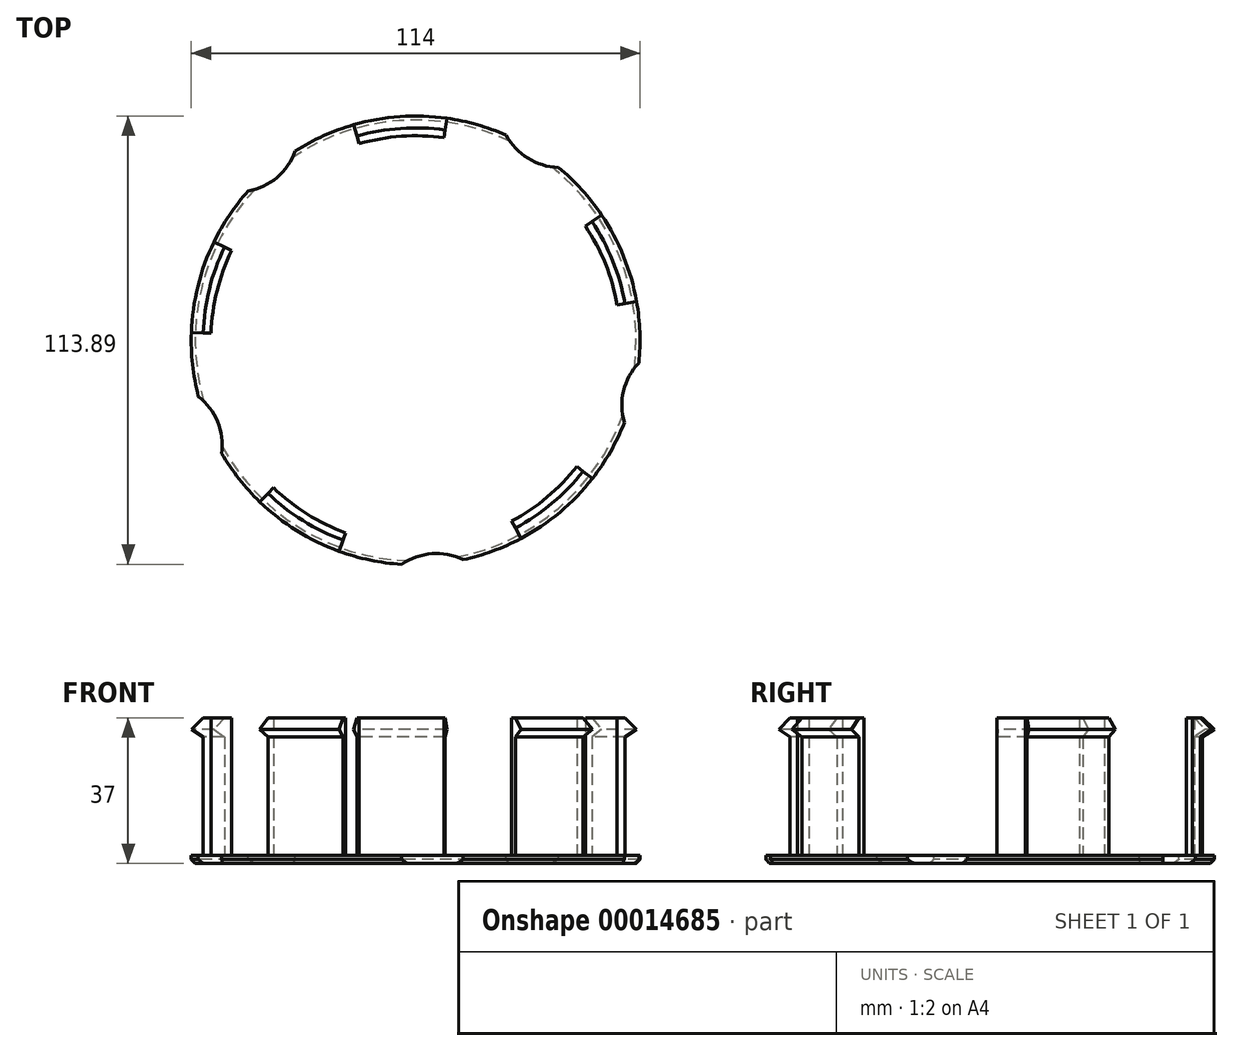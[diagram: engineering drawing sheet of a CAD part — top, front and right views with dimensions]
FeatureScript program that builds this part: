
annotation { "Feature Type Name" : "Feature", "Feature Type Description" : "" }
export const myFeature = defineFeature(function(context is Context, id is Id, definition is map)
    precondition{}
    {
        {
            var Q0;
            Q0=qCreatedBy(makeId("Top.planeOp"),FACE);
            var sketch = newSketch(context, id + "F0", { "sketchPlane" : qUnion([Q0])});
            skCircle(sketch, "E0", {"center": v(0, 0) * mm, "radius": 54 * mm});
            skCircle(sketch, "E1.0", {"center": v(0, 0) * mm, "radius": 52 * mm});
            skCircle(sketch, "E2.0", {"center": v(0, 0) * mm, "radius": 57 * mm});
            skLineSegment(sketch, "E3", {"start": v(0, 52) * mm, "end": v(0, 57) * mm});
            skLineSegment(sketch, "E4.1.0", {"start": v(-7.24, 51.5) * mm, "end": v(-7.93, 56.45) * mm});
            skLineSegment(sketch, "E4.2.0", {"start": v(-14.33, 49.99) * mm, "end": v(-15.71, 54.8) * mm});
            skLineSegment(sketch, "E4.3.0", {"start": v(-21.15, 47.5) * mm, "end": v(-23.18, 52.07) * mm});
            skLineSegment(sketch, "E4.4.0", {"start": v(-27.56, 44.1) * mm, "end": v(-30.2, 48.34) * mm});
            skLineSegment(sketch, "E4.5.0", {"start": v(-33.42, 39.83) * mm, "end": v(-36.64, 43.66) * mm});
            skLineSegment(sketch, "E4.6.0", {"start": v(-38.64, 34.8) * mm, "end": v(-42.36, 38.14) * mm});
            skLineSegment(sketch, "E4.7.0", {"start": v(-43.1, 29.08) * mm, "end": v(-47.26, 31.87) * mm});
            skLineSegment(sketch, "E4.8.0", {"start": v(-46.74, 22.8) * mm, "end": v(-51.23, 24.99) * mm});
            skLineSegment(sketch, "E4.9.0", {"start": v(-49.45, 16.07) * mm, "end": v(-54.21, 17.61) * mm});
            skLineSegment(sketch, "E5.1.10.0", {"start": v(-51.21, 9.03) * mm, "end": v(-56.13, 9.9) * mm});
            skLineSegment(sketch, "E5.1.11.0", {"start": v(-51.97, 1.81) * mm, "end": v(-56.97, 1.99) * mm});
            skLineSegment(sketch, "E5.1.12.0", {"start": v(-51.72, -5.44) * mm, "end": v(-56.69, -5.96) * mm});
            skLineSegment(sketch, "E5.1.13.0", {"start": v(-50.46, -12.58) * mm, "end": v(-55.3, -13.79) * mm});
            skLineSegment(sketch, "E5.1.14.0", {"start": v(-48.21, -19.48) * mm, "end": v(-52.85, -21.35) * mm});
            skLineSegment(sketch, "E5.1.15.0", {"start": v(-45.03, -26) * mm, "end": v(-49.36, -28.5) * mm});
            skLineSegment(sketch, "E5.1.16.0", {"start": v(-40.98, -32.01) * mm, "end": v(-44.92, -35.1) * mm});
            skLineSegment(sketch, "E5.1.17.0", {"start": v(-36.12, -37.4) * mm, "end": v(-39.6, -41) * mm});
            skLineSegment(sketch, "E5.1.18.0", {"start": v(-30.56, -42.07) * mm, "end": v(-33.5, -46.11) * mm});
            skLineSegment(sketch, "E5.1.19.0", {"start": v(-24.41, -45.91) * mm, "end": v(-26.76, -50.33) * mm});
            skLineSegment(sketch, "E6.1.20.0", {"start": v(-17.79, -48.86) * mm, "end": v(-19.5, -53.56) * mm});
            skLineSegment(sketch, "E6.1.21.0", {"start": v(-10.81, -50.86) * mm, "end": v(-11.85, -55.75) * mm});
            skLineSegment(sketch, "E6.1.22.0", {"start": v(-3.63, -51.87) * mm, "end": v(-3.98, -56.86) * mm});
            skLineSegment(sketch, "E6.1.23.0", {"start": v(3.63, -51.87) * mm, "end": v(3.98, -56.86) * mm});
            skLineSegment(sketch, "E6.1.24.0", {"start": v(10.81, -50.86) * mm, "end": v(11.85, -55.75) * mm});
            skLineSegment(sketch, "E7.1.25.0", {"start": v(17.79, -48.86) * mm, "end": v(19.5, -53.56) * mm});
            skLineSegment(sketch, "E8.1.26.0", {"start": v(24.41, -45.91) * mm, "end": v(26.76, -50.33) * mm});
            skLineSegment(sketch, "E8.1.27.0", {"start": v(30.56, -42.07) * mm, "end": v(33.5, -46.11) * mm});
            skLineSegment(sketch, "E8.1.28.0", {"start": v(36.12, -37.4) * mm, "end": v(39.6, -41) * mm});
            skLineSegment(sketch, "E8.1.29.0", {"start": v(40.98, -32.01) * mm, "end": v(44.92, -35.1) * mm});
            skLineSegment(sketch, "E9.1.30.0", {"start": v(45.03, -26) * mm, "end": v(49.36, -28.5) * mm});
            skLineSegment(sketch, "E9.1.31.0", {"start": v(48.21, -19.48) * mm, "end": v(52.85, -21.35) * mm});
            skLineSegment(sketch, "E9.1.32.0", {"start": v(50.46, -12.58) * mm, "end": v(55.3, -13.79) * mm});
            skLineSegment(sketch, "E9.1.33.0", {"start": v(51.72, -5.44) * mm, "end": v(56.69, -5.96) * mm});
            skLineSegment(sketch, "E9.1.34.0", {"start": v(51.97, 1.81) * mm, "end": v(56.97, 1.99) * mm});
            skLineSegment(sketch, "E10.1.35.0", {"start": v(51.21, 9.03) * mm, "end": v(56.13, 9.9) * mm});
            skLineSegment(sketch, "E10.1.36.0", {"start": v(49.45, 16.07) * mm, "end": v(54.21, 17.61) * mm});
            skLineSegment(sketch, "E10.1.37.0", {"start": v(46.74, 22.8) * mm, "end": v(51.23, 24.99) * mm});
            skLineSegment(sketch, "E10.1.38.0", {"start": v(43.1, 29.08) * mm, "end": v(47.26, 31.87) * mm});
            skLineSegment(sketch, "E10.1.39.0", {"start": v(38.64, 34.8) * mm, "end": v(42.36, 38.14) * mm});
            skCircle(sketch, "E11", {"center": v(36.65, 59.46) * mm, "radius": 15.5 * mm});
            skCircle(sketch, "E12.1.0", {"center": v(-45.23, 53.23) * mm, "radius": 15.5 * mm});
            skCircle(sketch, "E12.2.0", {"center": v(-64.6, -26.56) * mm, "radius": 15.5 * mm});
            skCircle(sketch, "E13.1.3.0", {"center": v(5.3, -69.65) * mm, "radius": 15.5 * mm});
            skCircle(sketch, "E13.1.4.0", {"center": v(67.88, -16.48) * mm, "radius": 15.5 * mm});
            skLineSegment(sketch, "E14.1.40.0", {"start": v(33.42, 39.83) * mm, "end": v(36.64, 43.66) * mm});
            skLineSegment(sketch, "E14.1.41.0", {"start": v(27.56, 44.1) * mm, "end": v(30.2, 48.34) * mm});
            skLineSegment(sketch, "E14.1.42.0", {"start": v(21.15, 47.5) * mm, "end": v(23.18, 52.07) * mm});
            skLineSegment(sketch, "E14.1.43.0", {"start": v(14.33, 49.99) * mm, "end": v(15.71, 54.8) * mm});
            skLineSegment(sketch, "E14.1.44.0", {"start": v(7.24, 51.5) * mm, "end": v(7.93, 56.45) * mm});
            skSolve(sketch);
        }
        {
            var Q0;
            {var subQ0=sQuery(id+"F0.wireOp",EDGE,"E3");var subQ1=sQuery(id+"F0.wireOp",EDGE,"E0");var subQ2=makeQuery(id+"F0.imprint","INTERSECT",VERTEX,{"derivedFrom":[subQ1,subQ0]});Q0=makeQuery(id+"F0.imprint","IMPRINT",FACE,{"disambiguationData":[TD([[makeQuery(id+"F0.imprint","IMPRINT",EDGE,{"disambiguationData":[TD([[subQ2,-1.0]])],"derivedFrom":subQ1}),1.0]])]});}
            var Q1;
            {var subQ1=sQuery(id+"F0.wireOp",EDGE,"E0");var subQ5=sQuery(id+"F0.wireOp",EDGE,"E4.1.0");var subQ6=makeQuery(id+"F0.imprint","INTERSECT",VERTEX,{"derivedFrom":[subQ1,subQ5]});Q1=makeQuery(id+"F0.imprint","IMPRINT",FACE,{"disambiguationData":[TD([[makeQuery(id+"F0.imprint","IMPRINT",EDGE,{"disambiguationData":[TD([[subQ6,-1.0]])],"derivedFrom":subQ1}),1.0]])]});}
            var Q2;
            {var subQ1=sQuery(id+"F0.wireOp",EDGE,"E0");var subQ5=sQuery(id+"F0.wireOp",EDGE,"E4.8.0");var subQ6=makeQuery(id+"F0.imprint","INTERSECT",VERTEX,{"derivedFrom":[subQ1,subQ5]});Q2=makeQuery(id+"F0.imprint","IMPRINT",FACE,{"disambiguationData":[TD([[makeQuery(id+"F0.imprint","IMPRINT",EDGE,{"disambiguationData":[TD([[subQ6,-1.0]])],"derivedFrom":subQ1}),1.0]])]});}
            var Q3;
            {var subQ1=sQuery(id+"F0.wireOp",EDGE,"E0");var subQ5=sQuery(id+"F0.wireOp",EDGE,"E3");var subQ6=makeQuery(id+"F0.imprint","INTERSECT",VERTEX,{"derivedFrom":[subQ1,subQ5]});Q3=makeQuery(id+"F0.imprint","IMPRINT",FACE,{"disambiguationData":[TD([[makeQuery(id+"F0.imprint","IMPRINT",EDGE,{"disambiguationData":[TD([[subQ6,-1.0]])],"derivedFrom":subQ1}),-1.0]])]});}
            var Q4;
            {var subQ1=sQuery(id+"F0.wireOp",EDGE,"E0");var subQ5=sQuery(id+"F0.wireOp",EDGE,"E4.1.0");var subQ6=makeQuery(id+"F0.imprint","INTERSECT",VERTEX,{"derivedFrom":[subQ1,subQ5]});Q4=makeQuery(id+"F0.imprint","IMPRINT",FACE,{"disambiguationData":[TD([[makeQuery(id+"F0.imprint","IMPRINT",EDGE,{"disambiguationData":[TD([[subQ6,-1.0]])],"derivedFrom":subQ1}),-1.0]])]});}
            var Q5;
            {var subQ0=sQuery(id+"F0.wireOp",EDGE,"E4.8.0");var subQ1=sQuery(id+"F0.wireOp",EDGE,"E0");var subQ2=makeQuery(id+"F0.imprint","INTERSECT",VERTEX,{"derivedFrom":[subQ1,subQ0]});Q5=makeQuery(id+"F0.imprint","IMPRINT",FACE,{"disambiguationData":[TD([[makeQuery(id+"F0.imprint","IMPRINT",EDGE,{"disambiguationData":[TD([[subQ2,-1.0]])],"derivedFrom":subQ1}),-1.0]])]});}
            var Q6;
            {var subQ1=sQuery(id+"F0.wireOp",EDGE,"E0");var subQ5=sQuery(id+"F0.wireOp",EDGE,"E4.9.0");var subQ6=makeQuery(id+"F0.imprint","INTERSECT",VERTEX,{"derivedFrom":[subQ1,subQ5]});Q6=makeQuery(id+"F0.imprint","IMPRINT",FACE,{"disambiguationData":[TD([[makeQuery(id+"F0.imprint","IMPRINT",EDGE,{"disambiguationData":[TD([[subQ6,-1.0]])],"derivedFrom":subQ1}),1.0]])]});}
            var Q7;
            {var subQ1=sQuery(id+"F0.wireOp",EDGE,"E0");var subQ5=sQuery(id+"F0.wireOp",EDGE,"E4.9.0");var subQ6=makeQuery(id+"F0.imprint","INTERSECT",VERTEX,{"derivedFrom":[subQ1,subQ5]});Q7=makeQuery(id+"F0.imprint","IMPRINT",FACE,{"disambiguationData":[TD([[makeQuery(id+"F0.imprint","IMPRINT",EDGE,{"disambiguationData":[TD([[subQ6,-1.0]])],"derivedFrom":subQ1}),-1.0]])]});}
            var Q8;
            {var subQ1=sQuery(id+"F0.wireOp",EDGE,"E0");var subQ5=sQuery(id+"F0.wireOp",EDGE,"E5.1.17.0");var subQ6=makeQuery(id+"F0.imprint","INTERSECT",VERTEX,{"derivedFrom":[subQ1,subQ5]});Q8=makeQuery(id+"F0.imprint","IMPRINT",FACE,{"disambiguationData":[TD([[makeQuery(id+"F0.imprint","IMPRINT",EDGE,{"disambiguationData":[TD([[subQ6,-1.0]])],"derivedFrom":subQ1}),-1.0]])]});}
            var Q9;
            {var subQ1=sQuery(id+"F0.wireOp",EDGE,"E0");var subQ5=sQuery(id+"F0.wireOp",EDGE,"E5.1.17.0");var subQ6=makeQuery(id+"F0.imprint","INTERSECT",VERTEX,{"derivedFrom":[subQ1,subQ5]});Q9=makeQuery(id+"F0.imprint","IMPRINT",FACE,{"disambiguationData":[TD([[makeQuery(id+"F0.imprint","IMPRINT",EDGE,{"disambiguationData":[TD([[subQ6,-1.0]])],"derivedFrom":subQ1}),1.0]])]});}
            var Q10;
            {var subQ1=sQuery(id+"F0.wireOp",EDGE,"E0");var subQ5=sQuery(id+"F0.wireOp",EDGE,"E5.1.10.0");var subQ6=makeQuery(id+"F0.imprint","INTERSECT",VERTEX,{"derivedFrom":[subQ1,subQ5]});Q10=makeQuery(id+"F0.imprint","IMPRINT",FACE,{"disambiguationData":[TD([[makeQuery(id+"F0.imprint","IMPRINT",EDGE,{"disambiguationData":[TD([[subQ6,-1.0]])],"derivedFrom":subQ1}),1.0]])]});}
            var Q11;
            {var subQ1=sQuery(id+"F0.wireOp",EDGE,"E0");var subQ5=sQuery(id+"F0.wireOp",EDGE,"E5.1.10.0");var subQ6=makeQuery(id+"F0.imprint","INTERSECT",VERTEX,{"derivedFrom":[subQ1,subQ5]});Q11=makeQuery(id+"F0.imprint","IMPRINT",FACE,{"disambiguationData":[TD([[makeQuery(id+"F0.imprint","IMPRINT",EDGE,{"disambiguationData":[TD([[subQ6,-1.0]])],"derivedFrom":subQ1}),-1.0]])]});}
            var Q12;
            {var subQ0=sQuery(id+"F0.wireOp",EDGE,"E14.1.44.0");var subQ1=sQuery(id+"F0.wireOp",EDGE,"E0");var subQ2=makeQuery(id+"F0.imprint","INTERSECT",VERTEX,{"derivedFrom":[subQ1,subQ0]});Q12=makeQuery(id+"F0.imprint","IMPRINT",FACE,{"disambiguationData":[TD([[makeQuery(id+"F0.imprint","IMPRINT",EDGE,{"disambiguationData":[TD([[subQ2,-1.0]])],"derivedFrom":subQ1}),1.0]])]});}
            var Q13;
            {var subQ0=sQuery(id+"F0.wireOp",EDGE,"E14.1.44.0");var subQ1=sQuery(id+"F0.wireOp",EDGE,"E0");var subQ2=makeQuery(id+"F0.imprint","INTERSECT",VERTEX,{"derivedFrom":[subQ1,subQ0]});Q13=makeQuery(id+"F0.imprint","IMPRINT",FACE,{"disambiguationData":[TD([[makeQuery(id+"F0.imprint","IMPRINT",EDGE,{"disambiguationData":[TD([[subQ2,-1.0]])],"derivedFrom":subQ1}),-1.0]])]});}
            var Q14;
            {var subQ1=sQuery(id+"F0.wireOp",EDGE,"E0");var subQ5=sQuery(id+"F0.wireOp",EDGE,"E10.1.37.0");var subQ6=makeQuery(id+"F0.imprint","INTERSECT",VERTEX,{"derivedFrom":[subQ1,subQ5]});Q14=makeQuery(id+"F0.imprint","IMPRINT",FACE,{"disambiguationData":[TD([[makeQuery(id+"F0.imprint","IMPRINT",EDGE,{"disambiguationData":[TD([[subQ6,-1.0]])],"derivedFrom":subQ1}),-1.0]])]});}
            var Q15;
            {var subQ1=sQuery(id+"F0.wireOp",EDGE,"E0");var subQ5=sQuery(id+"F0.wireOp",EDGE,"E10.1.37.0");var subQ6=makeQuery(id+"F0.imprint","INTERSECT",VERTEX,{"derivedFrom":[subQ1,subQ5]});Q15=makeQuery(id+"F0.imprint","IMPRINT",FACE,{"disambiguationData":[TD([[makeQuery(id+"F0.imprint","IMPRINT",EDGE,{"disambiguationData":[TD([[subQ6,-1.0]])],"derivedFrom":subQ1}),1.0]])]});}
            var Q16;
            {var subQ1=sQuery(id+"F0.wireOp",EDGE,"E0");var subQ5=sQuery(id+"F0.wireOp",EDGE,"E10.1.36.0");var subQ6=makeQuery(id+"F0.imprint","INTERSECT",VERTEX,{"derivedFrom":[subQ1,subQ5]});Q16=makeQuery(id+"F0.imprint","IMPRINT",FACE,{"disambiguationData":[TD([[makeQuery(id+"F0.imprint","IMPRINT",EDGE,{"disambiguationData":[TD([[subQ6,-1.0]])],"derivedFrom":subQ1}),-1.0]])]});}
            var Q17;
            {var subQ1=sQuery(id+"F0.wireOp",EDGE,"E0");var subQ5=sQuery(id+"F0.wireOp",EDGE,"E10.1.36.0");var subQ6=makeQuery(id+"F0.imprint","INTERSECT",VERTEX,{"derivedFrom":[subQ1,subQ5]});Q17=makeQuery(id+"F0.imprint","IMPRINT",FACE,{"disambiguationData":[TD([[makeQuery(id+"F0.imprint","IMPRINT",EDGE,{"disambiguationData":[TD([[subQ6,-1.0]])],"derivedFrom":subQ1}),1.0]])]});}
            var Q18;
            {var subQ1=sQuery(id+"F0.wireOp",EDGE,"E0");var subQ5=sQuery(id+"F0.wireOp",EDGE,"E10.1.35.0");var subQ6=makeQuery(id+"F0.imprint","INTERSECT",VERTEX,{"derivedFrom":[subQ1,subQ5]});Q18=makeQuery(id+"F0.imprint","IMPRINT",FACE,{"disambiguationData":[TD([[makeQuery(id+"F0.imprint","IMPRINT",EDGE,{"disambiguationData":[TD([[subQ6,-1.0]])],"derivedFrom":subQ1}),1.0]])]});}
            var Q19;
            {var subQ1=sQuery(id+"F0.wireOp",EDGE,"E0");var subQ5=sQuery(id+"F0.wireOp",EDGE,"E10.1.35.0");var subQ6=makeQuery(id+"F0.imprint","INTERSECT",VERTEX,{"derivedFrom":[subQ1,subQ5]});Q19=makeQuery(id+"F0.imprint","IMPRINT",FACE,{"disambiguationData":[TD([[makeQuery(id+"F0.imprint","IMPRINT",EDGE,{"disambiguationData":[TD([[subQ6,-1.0]])],"derivedFrom":subQ1}),-1.0]])]});}
            var Q20;
            {var subQ1=sQuery(id+"F0.wireOp",EDGE,"E0");var subQ5=sQuery(id+"F0.wireOp",EDGE,"E8.1.28.0");var subQ6=makeQuery(id+"F0.imprint","INTERSECT",VERTEX,{"derivedFrom":[subQ1,subQ5]});Q20=makeQuery(id+"F0.imprint","IMPRINT",FACE,{"disambiguationData":[TD([[makeQuery(id+"F0.imprint","IMPRINT",EDGE,{"disambiguationData":[TD([[subQ6,-1.0]])],"derivedFrom":subQ1}),-1.0]])]});}
            var Q21;
            {var subQ0=sQuery(id+"F0.wireOp",EDGE,"E8.1.28.0");var subQ1=sQuery(id+"F0.wireOp",EDGE,"E0");var subQ2=makeQuery(id+"F0.imprint","INTERSECT",VERTEX,{"derivedFrom":[subQ1,subQ0]});Q21=makeQuery(id+"F0.imprint","IMPRINT",FACE,{"disambiguationData":[TD([[makeQuery(id+"F0.imprint","IMPRINT",EDGE,{"disambiguationData":[TD([[subQ2,-1.0]])],"derivedFrom":subQ1}),1.0]])]});}
            var Q22;
            {var subQ1=sQuery(id+"F0.wireOp",EDGE,"E0");var subQ5=sQuery(id+"F0.wireOp",EDGE,"E8.1.27.0");var subQ6=makeQuery(id+"F0.imprint","INTERSECT",VERTEX,{"derivedFrom":[subQ1,subQ5]});Q22=makeQuery(id+"F0.imprint","IMPRINT",FACE,{"disambiguationData":[TD([[makeQuery(id+"F0.imprint","IMPRINT",EDGE,{"disambiguationData":[TD([[subQ6,-1.0]])],"derivedFrom":subQ1}),1.0]])]});}
            var Q23;
            {var subQ1=sQuery(id+"F0.wireOp",EDGE,"E0");var subQ5=sQuery(id+"F0.wireOp",EDGE,"E8.1.27.0");var subQ6=makeQuery(id+"F0.imprint","INTERSECT",VERTEX,{"derivedFrom":[subQ1,subQ5]});Q23=makeQuery(id+"F0.imprint","IMPRINT",FACE,{"disambiguationData":[TD([[makeQuery(id+"F0.imprint","IMPRINT",EDGE,{"disambiguationData":[TD([[subQ6,-1.0]])],"derivedFrom":subQ1}),-1.0]])]});}
            var Q24;
            {var subQ1=sQuery(id+"F0.wireOp",EDGE,"E0");var subQ5=sQuery(id+"F0.wireOp",EDGE,"E8.1.26.0");var subQ6=makeQuery(id+"F0.imprint","INTERSECT",VERTEX,{"derivedFrom":[subQ1,subQ5]});Q24=makeQuery(id+"F0.imprint","IMPRINT",FACE,{"disambiguationData":[TD([[makeQuery(id+"F0.imprint","IMPRINT",EDGE,{"disambiguationData":[TD([[subQ6,-1.0]])],"derivedFrom":subQ1}),-1.0]])]});}
            var Q25;
            {var subQ1=sQuery(id+"F0.wireOp",EDGE,"E0");var subQ5=sQuery(id+"F0.wireOp",EDGE,"E8.1.26.0");var subQ7=makeQuery(id+"F0.imprint","INTERSECT",VERTEX,{"derivedFrom":[subQ1,subQ5]});Q25=makeQuery(id+"F0.imprint","IMPRINT",FACE,{"disambiguationData":[TD([[makeQuery(id+"F0.imprint","IMPRINT",EDGE,{"disambiguationData":[TD([[subQ7,-1.0]])],"derivedFrom":subQ1}),1.0]])]});}
            var Q26;
            {var subQ1=sQuery(id+"F0.wireOp",EDGE,"E0");var subQ5=sQuery(id+"F0.wireOp",EDGE,"E5.1.19.0");var subQ6=makeQuery(id+"F0.imprint","INTERSECT",VERTEX,{"derivedFrom":[subQ1,subQ5]});Q26=makeQuery(id+"F0.imprint","IMPRINT",FACE,{"disambiguationData":[TD([[makeQuery(id+"F0.imprint","IMPRINT",EDGE,{"disambiguationData":[TD([[subQ6,-1.0]])],"derivedFrom":subQ1}),-1.0]])]});}
            var Q27;
            {var subQ1=sQuery(id+"F0.wireOp",EDGE,"E0");var subQ5=sQuery(id+"F0.wireOp",EDGE,"E5.1.19.0");var subQ6=makeQuery(id+"F0.imprint","INTERSECT",VERTEX,{"derivedFrom":[subQ1,subQ5]});Q27=makeQuery(id+"F0.imprint","IMPRINT",FACE,{"disambiguationData":[TD([[makeQuery(id+"F0.imprint","IMPRINT",EDGE,{"disambiguationData":[TD([[subQ6,-1.0]])],"derivedFrom":subQ1}),1.0]])]});}
            var Q28;
            {var subQ1=sQuery(id+"F0.wireOp",EDGE,"E0");var subQ5=sQuery(id+"F0.wireOp",EDGE,"E5.1.18.0");var subQ6=makeQuery(id+"F0.imprint","INTERSECT",VERTEX,{"derivedFrom":[subQ1,subQ5]});Q28=makeQuery(id+"F0.imprint","IMPRINT",FACE,{"disambiguationData":[TD([[makeQuery(id+"F0.imprint","IMPRINT",EDGE,{"disambiguationData":[TD([[subQ6,-1.0]])],"derivedFrom":subQ1}),1.0]])]});}
            var Q29;
            {var subQ1=sQuery(id+"F0.wireOp",EDGE,"E0");var subQ5=sQuery(id+"F0.wireOp",EDGE,"E5.1.18.0");var subQ6=makeQuery(id+"F0.imprint","INTERSECT",VERTEX,{"derivedFrom":[subQ1,subQ5]});Q29=makeQuery(id+"F0.imprint","IMPRINT",FACE,{"disambiguationData":[TD([[makeQuery(id+"F0.imprint","IMPRINT",EDGE,{"disambiguationData":[TD([[subQ6,-1.0]])],"derivedFrom":subQ1}),-1.0]])]});}
            extrude(context, id + "F1", {"entities" : qUnion([Q0, Q1, Q2, Q3, Q4, Q5, Q6, Q7, Q8, Q9, Q10, Q11, Q12, Q13, Q14, Q15, Q16, Q17, Q18, Q19, Q20, Q21, Q22, Q23, Q24, Q25, Q26, Q27, Q28, Q29]), "depth" : 35 * mm});
        }
        {
            var Q0;
            Q0=makeQuery(id+"F0.imprint","IMPRINT",FACE,{"disambiguationData":[TD([[makeQuery(id+"F0.imprint","IMPRINT",EDGE,{"derivedFrom":sQuery(id+"F0.wireOp",EDGE,"E0")}),-1.0]])]});
            var Q1;
            Q1=makeQuery(id+"F0.imprint","IMPRINT",FACE,{"disambiguationData":[TD([[makeQuery(id+"F0.imprint","IMPRINT",EDGE,{"derivedFrom":sQuery(id+"F0.wireOp",EDGE,"E0")}),1.0]])]});
            var Q2;
            Q2=makeQuery(id+"F0.imprint","IMPRINT",FACE,{"disambiguationData":[TD([[makeQuery(id+"F0.imprint","IMPRINT",EDGE,{"derivedFrom":sQuery(id+"F0.wireOp",EDGE,"6aa7c3f9-1c9a-4405-8abc-e9495ce803aa.0")}),1.0]])]});
            var Q3;
            {var subQ5=sQuery(id+"F0.wireOp",EDGE,"E0");var subQ7=sQuery(id+"F0.wireOp",EDGE,"E5.1.11.0");var subQ8=makeQuery(id+"F0.imprint","INTERSECT",VERTEX,{"derivedFrom":[subQ5,subQ7]});Q3=makeQuery(id+"F0.imprint","IMPRINT",FACE,{"disambiguationData":[TD([[makeQuery(id+"F0.imprint","IMPRINT",EDGE,{"disambiguationData":[TD([[subQ8,-1.0]])],"derivedFrom":subQ5}),-1.0]])]});}
            var Q4;
            {var subQ1=sQuery(id+"F0.wireOp",EDGE,"E5.1.13.0");var subQ6=sQuery(id+"F0.wireOp",EDGE,"E0");var subQ9=makeQuery(id+"F0.imprint","INTERSECT",VERTEX,{"derivedFrom":[subQ6,subQ1]});Q4=makeQuery(id+"F0.imprint","IMPRINT",FACE,{"disambiguationData":[TD([[makeQuery(id+"F0.imprint","IMPRINT",EDGE,{"disambiguationData":[TD([[subQ9,-1.0]])],"derivedFrom":subQ6}),-1.0]])]});}
            var Q5;
            {var subQ5=sQuery(id+"F0.wireOp",EDGE,"E0");var subQ7=sQuery(id+"F0.wireOp",EDGE,"E5.1.19.0");var subQ8=makeQuery(id+"F0.imprint","INTERSECT",VERTEX,{"derivedFrom":[subQ5,subQ7]});Q5=makeQuery(id+"F0.imprint","IMPRINT",FACE,{"disambiguationData":[TD([[makeQuery(id+"F0.imprint","IMPRINT",EDGE,{"disambiguationData":[TD([[subQ8,-1.0]])],"derivedFrom":subQ5}),-1.0]])]});}
            var Q6;
            {var subQ1=sQuery(id+"F0.wireOp",EDGE,"E6.1.21.0");var subQ6=sQuery(id+"F0.wireOp",EDGE,"E0");var subQ9=makeQuery(id+"F0.imprint","INTERSECT",VERTEX,{"derivedFrom":[subQ6,subQ1]});Q6=makeQuery(id+"F0.imprint","IMPRINT",FACE,{"disambiguationData":[TD([[makeQuery(id+"F0.imprint","IMPRINT",EDGE,{"disambiguationData":[TD([[subQ9,-1.0]])],"derivedFrom":subQ6}),-1.0]])]});}
            var Q7;
            {var subQ5=sQuery(id+"F0.wireOp",EDGE,"E0");var subQ7=sQuery(id+"F0.wireOp",EDGE,"E8.1.27.0");var subQ8=makeQuery(id+"F0.imprint","INTERSECT",VERTEX,{"derivedFrom":[subQ5,subQ7]});Q7=makeQuery(id+"F0.imprint","IMPRINT",FACE,{"disambiguationData":[TD([[makeQuery(id+"F0.imprint","IMPRINT",EDGE,{"disambiguationData":[TD([[subQ8,-1.0]])],"derivedFrom":subQ5}),-1.0]])]});}
            var Q8;
            {var subQ0=sQuery(id+"F0.wireOp",EDGE,"E9.1.30.0");var subQ1=sQuery(id+"F0.wireOp",EDGE,"E0");var subQ2=makeQuery(id+"F0.imprint","INTERSECT",VERTEX,{"derivedFrom":[subQ1,subQ0]});Q8=makeQuery(id+"F0.imprint","IMPRINT",FACE,{"disambiguationData":[TD([[makeQuery(id+"F0.imprint","IMPRINT",EDGE,{"disambiguationData":[TD([[subQ2,1.0]])],"derivedFrom":subQ1}),-1.0]])]});}
            var Q9;
            {var subQ5=sQuery(id+"F0.wireOp",EDGE,"E0");var subQ7=sQuery(id+"F0.wireOp",EDGE,"E10.1.35.0");var subQ8=makeQuery(id+"F0.imprint","INTERSECT",VERTEX,{"derivedFrom":[subQ5,subQ7]});Q9=makeQuery(id+"F0.imprint","IMPRINT",FACE,{"disambiguationData":[TD([[makeQuery(id+"F0.imprint","IMPRINT",EDGE,{"disambiguationData":[TD([[subQ8,-1.0]])],"derivedFrom":subQ5}),-1.0]])]});}
            var Q10;
            {var subQ1=sQuery(id+"F0.wireOp",EDGE,"E10.1.37.0");var subQ6=sQuery(id+"F0.wireOp",EDGE,"E0");var subQ9=makeQuery(id+"F0.imprint","INTERSECT",VERTEX,{"derivedFrom":[subQ6,subQ1]});Q10=makeQuery(id+"F0.imprint","IMPRINT",FACE,{"disambiguationData":[TD([[makeQuery(id+"F0.imprint","IMPRINT",EDGE,{"disambiguationData":[TD([[subQ9,-1.0]])],"derivedFrom":subQ6}),-1.0]])]});}
            var Q11;
            {var subQ5=sQuery(id+"F0.wireOp",EDGE,"E0");var subQ7=sQuery(id+"F0.wireOp",EDGE,"E4.3.0");var subQ8=makeQuery(id+"F0.imprint","INTERSECT",VERTEX,{"derivedFrom":[subQ5,subQ7]});Q11=makeQuery(id+"F0.imprint","IMPRINT",FACE,{"disambiguationData":[TD([[makeQuery(id+"F0.imprint","IMPRINT",EDGE,{"disambiguationData":[TD([[subQ8,-1.0]])],"derivedFrom":subQ5}),-1.0]])]});}
            var Q12;
            {var subQ1=sQuery(id+"F0.wireOp",EDGE,"E0");var subQ5=sQuery(id+"F0.wireOp",EDGE,"E4.5.0");var subQ8=makeQuery(id+"F0.imprint","INTERSECT",VERTEX,{"derivedFrom":[subQ1,subQ5]});Q12=makeQuery(id+"F0.imprint","IMPRINT",FACE,{"disambiguationData":[TD([[makeQuery(id+"F0.imprint","IMPRINT",EDGE,{"disambiguationData":[TD([[subQ8,-1.0]])],"derivedFrom":subQ1}),-1.0]])]});}
            var Q13;
            {var subQ1=sQuery(id+"F0.wireOp",EDGE,"E4.6.0");var subQ6=sQuery(id+"F0.wireOp",EDGE,"E0");var subQ9=makeQuery(id+"F0.imprint","INTERSECT",VERTEX,{"derivedFrom":[subQ6,subQ1]});Q13=makeQuery(id+"F0.imprint","IMPRINT",FACE,{"disambiguationData":[TD([[makeQuery(id+"F0.imprint","IMPRINT",EDGE,{"disambiguationData":[TD([[subQ9,-1.0]])],"derivedFrom":subQ6}),-1.0]])]});}
            var Q14;
            {var subQ5=sQuery(id+"F0.wireOp",EDGE,"E0");var subQ7=sQuery(id+"F0.wireOp",EDGE,"E4.4.0");var subQ8=makeQuery(id+"F0.imprint","INTERSECT",VERTEX,{"derivedFrom":[subQ5,subQ7]});Q14=makeQuery(id+"F0.imprint","IMPRINT",FACE,{"disambiguationData":[TD([[makeQuery(id+"F0.imprint","IMPRINT",EDGE,{"disambiguationData":[TD([[subQ8,-1.0]])],"derivedFrom":subQ5}),-1.0]])]});}
            var Q15;
            {var subQ1=sQuery(id+"F0.wireOp",EDGE,"E0");var subQ5=sQuery(id+"F0.wireOp",EDGE,"E14.1.42.0");var subQ8=makeQuery(id+"F0.imprint","INTERSECT",VERTEX,{"derivedFrom":[subQ1,subQ5]});Q15=makeQuery(id+"F0.imprint","IMPRINT",FACE,{"disambiguationData":[TD([[makeQuery(id+"F0.imprint","IMPRINT",EDGE,{"disambiguationData":[TD([[subQ8,-1.0]])],"derivedFrom":subQ1}),-1.0]])]});}
            var Q16;
            {var subQ3=sQuery(id+"F0.wireOp",EDGE,"E0");var subQ5=sQuery(id+"F0.wireOp",EDGE,"E14.1.40.0");var subQ6=makeQuery(id+"F0.imprint","INTERSECT",VERTEX,{"derivedFrom":[subQ3,subQ5]});Q16=makeQuery(id+"F0.imprint","IMPRINT",FACE,{"disambiguationData":[TD([[makeQuery(id+"F0.imprint","IMPRINT",EDGE,{"disambiguationData":[TD([[subQ6,-1.0]])],"derivedFrom":subQ3}),-1.0]])]});}
            var Q17;
            {var subQ1=sQuery(id+"F0.wireOp",EDGE,"E6.1.24.0");var subQ6=sQuery(id+"F0.wireOp",EDGE,"E0");var subQ9=makeQuery(id+"F0.imprint","INTERSECT",VERTEX,{"derivedFrom":[subQ6,subQ1]});Q17=makeQuery(id+"F0.imprint","IMPRINT",FACE,{"disambiguationData":[TD([[makeQuery(id+"F0.imprint","IMPRINT",EDGE,{"disambiguationData":[TD([[subQ9,-1.0]])],"derivedFrom":subQ6}),-1.0]])]});}
            var Q18;
            {var subQ5=sQuery(id+"F0.wireOp",EDGE,"E0");var subQ7=sQuery(id+"F0.wireOp",EDGE,"E6.1.22.0");var subQ8=makeQuery(id+"F0.imprint","INTERSECT",VERTEX,{"derivedFrom":[subQ5,subQ7]});Q18=makeQuery(id+"F0.imprint","IMPRINT",FACE,{"disambiguationData":[TD([[makeQuery(id+"F0.imprint","IMPRINT",EDGE,{"disambiguationData":[TD([[subQ8,-1.0]])],"derivedFrom":subQ5}),-1.0]])]});}
            var Q19;
            {var subQ1=sQuery(id+"F0.wireOp",EDGE,"E5.1.15.0");var subQ6=sQuery(id+"F0.wireOp",EDGE,"E0");var subQ9=makeQuery(id+"F0.imprint","INTERSECT",VERTEX,{"derivedFrom":[subQ6,subQ1]});Q19=makeQuery(id+"F0.imprint","IMPRINT",FACE,{"disambiguationData":[TD([[makeQuery(id+"F0.imprint","IMPRINT",EDGE,{"disambiguationData":[TD([[subQ9,-1.0]])],"derivedFrom":subQ6}),-1.0]])]});}
            var Q20;
            {var subQ5=sQuery(id+"F0.wireOp",EDGE,"E0");var subQ7=sQuery(id+"F0.wireOp",EDGE,"E9.1.31.0");var subQ8=makeQuery(id+"F0.imprint","INTERSECT",VERTEX,{"derivedFrom":[subQ5,subQ7]});Q20=makeQuery(id+"F0.imprint","IMPRINT",FACE,{"disambiguationData":[TD([[makeQuery(id+"F0.imprint","IMPRINT",EDGE,{"disambiguationData":[TD([[subQ8,-1.0]])],"derivedFrom":subQ5}),-1.0]])]});}
            var Q21;
            {var subQ5=sQuery(id+"F0.wireOp",EDGE,"E9.1.34.0");var subQ6=sQuery(id+"F0.wireOp",EDGE,"E0");var subQ7=makeQuery(id+"F0.imprint","INTERSECT",VERTEX,{"derivedFrom":[subQ6,subQ5]});Q21=makeQuery(id+"F0.imprint","IMPRINT",FACE,{"disambiguationData":[TD([[makeQuery(id+"F0.imprint","IMPRINT",EDGE,{"disambiguationData":[TD([[subQ7,1.0]])],"derivedFrom":subQ6}),-1.0]])]});}
            var Q22;
            {var subQ0=sQuery(id+"F0.wireOp",EDGE,"E1.0");var subQ1=makeQuery(id+"F0.imprint","INTERSECT",VERTEX,{"derivedFrom":[subQ0,sQuery(id+"F0.wireOp",EDGE,"E9.1.34.0")]});Q22=makeQuery(id+"F0.imprint","IMPRINT",FACE,{"disambiguationData":[TD([[makeQuery(id+"F0.imprint","IMPRINT",EDGE,{"disambiguationData":[TD([[subQ1,-1.0]])],"derivedFrom":subQ0}),1.0]])]});}
            var Q23;
            {var subQ1=sQuery(id+"F0.wireOp",EDGE,"E5.1.14.0");var subQ6=sQuery(id+"F0.wireOp",EDGE,"E0");var subQ9=makeQuery(id+"F0.imprint","INTERSECT",VERTEX,{"derivedFrom":[subQ6,subQ1]});Q23=makeQuery(id+"F0.imprint","IMPRINT",FACE,{"disambiguationData":[TD([[makeQuery(id+"F0.imprint","IMPRINT",EDGE,{"disambiguationData":[TD([[subQ9,-1.0]])],"derivedFrom":subQ6}),-1.0]])]});}
            var Q24;
            {var subQ1=sQuery(id+"F0.wireOp",EDGE,"E6.1.23.0");var subQ6=sQuery(id+"F0.wireOp",EDGE,"E0");var subQ9=makeQuery(id+"F0.imprint","INTERSECT",VERTEX,{"derivedFrom":[subQ6,subQ1]});Q24=makeQuery(id+"F0.imprint","IMPRINT",FACE,{"disambiguationData":[TD([[makeQuery(id+"F0.imprint","IMPRINT",EDGE,{"disambiguationData":[TD([[subQ9,-1.0]])],"derivedFrom":subQ6}),-1.0]])]});}
            var Q25;
            {var subQ1=sQuery(id+"F0.wireOp",EDGE,"E9.1.32.0");var subQ5=sQuery(id+"F0.wireOp",EDGE,"E0");var subQ6=makeQuery(id+"F0.imprint","INTERSECT",VERTEX,{"derivedFrom":[subQ5,subQ1]});Q25=makeQuery(id+"F0.imprint","IMPRINT",FACE,{"disambiguationData":[TD([[makeQuery(id+"F0.imprint","IMPRINT",EDGE,{"disambiguationData":[TD([[subQ6,-1.0]])],"derivedFrom":subQ5}),-1.0]])]});}
            var Q26;
            {var subQ1=sQuery(id+"F0.wireOp",EDGE,"E0");var subQ5=sQuery(id+"F0.wireOp",EDGE,"E14.1.41.0");var subQ8=makeQuery(id+"F0.imprint","INTERSECT",VERTEX,{"derivedFrom":[subQ1,subQ5]});Q26=makeQuery(id+"F0.imprint","IMPRINT",FACE,{"disambiguationData":[TD([[makeQuery(id+"F0.imprint","IMPRINT",EDGE,{"disambiguationData":[TD([[subQ8,-1.0]])],"derivedFrom":subQ1}),-1.0]])]});}
            extrude(context, id + "F2", {"entities" : qUnion([Q0, Q1, Q2, Q3, Q4, Q5, Q6, Q7, Q8, Q9, Q10, Q11, Q12, Q13, Q14, Q15, Q16, Q17, Q18, Q19, Q20, Q21, Q22, Q23, Q24, Q25, Q26]), "operationType" : NewBodyOperationType.ADD, "oppositeDirection" : true, "depth" : 2 * mm});
        }
        {
            var Q0;
            {var subQ1=sQuery(id+"F0.wireOp",EDGE,"E0");var subQ5=sQuery(id+"F0.wireOp",EDGE,"E10.1.35.0");var subQ6=makeQuery(id+"F0.imprint","INTERSECT",VERTEX,{"derivedFrom":[subQ1,subQ5]});Q0=makeQuery(id+"F0.imprint","IMPRINT",FACE,{"disambiguationData":[TD([[makeQuery(id+"F0.imprint","IMPRINT",EDGE,{"disambiguationData":[TD([[subQ6,-1.0]])],"derivedFrom":subQ1}),-1.0]])]});}
            var Q1;
            {var subQ1=sQuery(id+"F0.wireOp",EDGE,"E0");var subQ5=sQuery(id+"F0.wireOp",EDGE,"E10.1.36.0");var subQ6=makeQuery(id+"F0.imprint","INTERSECT",VERTEX,{"derivedFrom":[subQ1,subQ5]});Q1=makeQuery(id+"F0.imprint","IMPRINT",FACE,{"disambiguationData":[TD([[makeQuery(id+"F0.imprint","IMPRINT",EDGE,{"disambiguationData":[TD([[subQ6,-1.0]])],"derivedFrom":subQ1}),-1.0]])]});}
            var Q2;
            {var subQ1=sQuery(id+"F0.wireOp",EDGE,"E0");var subQ5=sQuery(id+"F0.wireOp",EDGE,"E10.1.37.0");var subQ6=makeQuery(id+"F0.imprint","INTERSECT",VERTEX,{"derivedFrom":[subQ1,subQ5]});Q2=makeQuery(id+"F0.imprint","IMPRINT",FACE,{"disambiguationData":[TD([[makeQuery(id+"F0.imprint","IMPRINT",EDGE,{"disambiguationData":[TD([[subQ6,-1.0]])],"derivedFrom":subQ1}),-1.0]])]});}
            var Q3;
            {var subQ0=sQuery(id+"F0.wireOp",EDGE,"E14.1.44.0");var subQ1=sQuery(id+"F0.wireOp",EDGE,"E0");var subQ2=makeQuery(id+"F0.imprint","INTERSECT",VERTEX,{"derivedFrom":[subQ1,subQ0]});Q3=makeQuery(id+"F0.imprint","IMPRINT",FACE,{"disambiguationData":[TD([[makeQuery(id+"F0.imprint","IMPRINT",EDGE,{"disambiguationData":[TD([[subQ2,-1.0]])],"derivedFrom":subQ1}),-1.0]])]});}
            var Q4;
            {var subQ1=sQuery(id+"F0.wireOp",EDGE,"E0");var subQ5=sQuery(id+"F0.wireOp",EDGE,"E3");var subQ6=makeQuery(id+"F0.imprint","INTERSECT",VERTEX,{"derivedFrom":[subQ1,subQ5]});Q4=makeQuery(id+"F0.imprint","IMPRINT",FACE,{"disambiguationData":[TD([[makeQuery(id+"F0.imprint","IMPRINT",EDGE,{"disambiguationData":[TD([[subQ6,-1.0]])],"derivedFrom":subQ1}),-1.0]])]});}
            var Q5;
            {var subQ1=sQuery(id+"F0.wireOp",EDGE,"E0");var subQ5=sQuery(id+"F0.wireOp",EDGE,"E4.1.0");var subQ6=makeQuery(id+"F0.imprint","INTERSECT",VERTEX,{"derivedFrom":[subQ1,subQ5]});Q5=makeQuery(id+"F0.imprint","IMPRINT",FACE,{"disambiguationData":[TD([[makeQuery(id+"F0.imprint","IMPRINT",EDGE,{"disambiguationData":[TD([[subQ6,-1.0]])],"derivedFrom":subQ1}),-1.0]])]});}
            var Q6;
            {var subQ1=sQuery(id+"F0.wireOp",EDGE,"E0");var subQ5=sQuery(id+"F0.wireOp",EDGE,"E4.8.0");var subQ6=makeQuery(id+"F0.imprint","INTERSECT",VERTEX,{"derivedFrom":[subQ1,subQ5]});Q6=makeQuery(id+"F0.imprint","IMPRINT",FACE,{"disambiguationData":[TD([[makeQuery(id+"F0.imprint","IMPRINT",EDGE,{"disambiguationData":[TD([[subQ6,-1.0]])],"derivedFrom":subQ1}),-1.0]])]});}
            var Q7;
            {var subQ1=sQuery(id+"F0.wireOp",EDGE,"E0");var subQ5=sQuery(id+"F0.wireOp",EDGE,"E4.9.0");var subQ6=makeQuery(id+"F0.imprint","INTERSECT",VERTEX,{"derivedFrom":[subQ1,subQ5]});Q7=makeQuery(id+"F0.imprint","IMPRINT",FACE,{"disambiguationData":[TD([[makeQuery(id+"F0.imprint","IMPRINT",EDGE,{"disambiguationData":[TD([[subQ6,-1.0]])],"derivedFrom":subQ1}),-1.0]])]});}
            var Q8;
            {var subQ1=sQuery(id+"F0.wireOp",EDGE,"E0");var subQ5=sQuery(id+"F0.wireOp",EDGE,"E5.1.10.0");var subQ6=makeQuery(id+"F0.imprint","INTERSECT",VERTEX,{"derivedFrom":[subQ1,subQ5]});Q8=makeQuery(id+"F0.imprint","IMPRINT",FACE,{"disambiguationData":[TD([[makeQuery(id+"F0.imprint","IMPRINT",EDGE,{"disambiguationData":[TD([[subQ6,-1.0]])],"derivedFrom":subQ1}),-1.0]])]});}
            var Q9;
            {var subQ1=sQuery(id+"F0.wireOp",EDGE,"E0");var subQ5=sQuery(id+"F0.wireOp",EDGE,"E5.1.17.0");var subQ6=makeQuery(id+"F0.imprint","INTERSECT",VERTEX,{"derivedFrom":[subQ1,subQ5]});Q9=makeQuery(id+"F0.imprint","IMPRINT",FACE,{"disambiguationData":[TD([[makeQuery(id+"F0.imprint","IMPRINT",EDGE,{"disambiguationData":[TD([[subQ6,-1.0]])],"derivedFrom":subQ1}),-1.0]])]});}
            var Q10;
            {var subQ1=sQuery(id+"F0.wireOp",EDGE,"E0");var subQ5=sQuery(id+"F0.wireOp",EDGE,"E5.1.18.0");var subQ6=makeQuery(id+"F0.imprint","INTERSECT",VERTEX,{"derivedFrom":[subQ1,subQ5]});Q10=makeQuery(id+"F0.imprint","IMPRINT",FACE,{"disambiguationData":[TD([[makeQuery(id+"F0.imprint","IMPRINT",EDGE,{"disambiguationData":[TD([[subQ6,-1.0]])],"derivedFrom":subQ1}),-1.0]])]});}
            var Q11;
            {var subQ1=sQuery(id+"F0.wireOp",EDGE,"E0");var subQ5=sQuery(id+"F0.wireOp",EDGE,"E5.1.19.0");var subQ6=makeQuery(id+"F0.imprint","INTERSECT",VERTEX,{"derivedFrom":[subQ1,subQ5]});Q11=makeQuery(id+"F0.imprint","IMPRINT",FACE,{"disambiguationData":[TD([[makeQuery(id+"F0.imprint","IMPRINT",EDGE,{"disambiguationData":[TD([[subQ6,-1.0]])],"derivedFrom":subQ1}),-1.0]])]});}
            var Q12;
            {var subQ1=sQuery(id+"F0.wireOp",EDGE,"E0");var subQ5=sQuery(id+"F0.wireOp",EDGE,"E8.1.26.0");var subQ6=makeQuery(id+"F0.imprint","INTERSECT",VERTEX,{"derivedFrom":[subQ1,subQ5]});Q12=makeQuery(id+"F0.imprint","IMPRINT",FACE,{"disambiguationData":[TD([[makeQuery(id+"F0.imprint","IMPRINT",EDGE,{"disambiguationData":[TD([[subQ6,-1.0]])],"derivedFrom":subQ1}),-1.0]])]});}
            var Q13;
            {var subQ1=sQuery(id+"F0.wireOp",EDGE,"E0");var subQ5=sQuery(id+"F0.wireOp",EDGE,"E8.1.27.0");var subQ6=makeQuery(id+"F0.imprint","INTERSECT",VERTEX,{"derivedFrom":[subQ1,subQ5]});Q13=makeQuery(id+"F0.imprint","IMPRINT",FACE,{"disambiguationData":[TD([[makeQuery(id+"F0.imprint","IMPRINT",EDGE,{"disambiguationData":[TD([[subQ6,-1.0]])],"derivedFrom":subQ1}),-1.0]])]});}
            var Q14;
            {var subQ1=sQuery(id+"F0.wireOp",EDGE,"E0");var subQ5=sQuery(id+"F0.wireOp",EDGE,"E8.1.28.0");var subQ6=makeQuery(id+"F0.imprint","INTERSECT",VERTEX,{"derivedFrom":[subQ1,subQ5]});Q14=makeQuery(id+"F0.imprint","IMPRINT",FACE,{"disambiguationData":[TD([[makeQuery(id+"F0.imprint","IMPRINT",EDGE,{"disambiguationData":[TD([[subQ6,-1.0]])],"derivedFrom":subQ1}),-1.0]])]});}
            var Q15;
            Q15=sQuery(id+"F0.wireOp",EDGE,"E2.0");
            extrude(context, id + "F3", {"entities" : qUnion([Q0, Q1, Q2, Q3, Q4, Q5, Q6, Q7, Q8, Q9, Q10, Q11, Q12, Q13, Q14]), "operationType" : NewBodyOperationType.REMOVE, "surfaceEntities" : qUnion([Q15]), "depth" : 32 * mm});
        }
        {
            var Q0;
            Q0=makeQuery(id+"F1.opExtrude","CAP_EDGE",EDGE,{"disambiguationData":[OSD([sQuery(id+"F0.wireOp",EDGE,"E2.0")])],"isStart":false});
            chamfer(context, id + "F4", {"entities" : qUnion([Q0]), "width" : 3 * mm, "tangentPropagation" : true});
        }
        {
            var Q0;
            {var subQ0=sQuery(id+"F0.wireOp",EDGE,"E2.0");var subQ1=makeQuery(id+"F0.imprint","INTERSECT",VERTEX,{"derivedFrom":[subQ0,sQuery(id+"F0.wireOp",EDGE,"E5.1.16.0")]});var subQ2=makeQuery(id+"F0.imprint","INTERSECT",VERTEX,{"derivedFrom":[subQ0,sQuery(id+"F0.wireOp",EDGE,"E5.1.17.0")]});var subQ3=makeQuery(id+"F0.imprint","INTERSECT",VERTEX,{"derivedFrom":[subQ0,sQuery(id+"F0.wireOp",EDGE,"E5.1.18.0")]});var subQ4=makeQuery(id+"F0.imprint","INTERSECT",VERTEX,{"derivedFrom":[subQ0,sQuery(id+"F0.wireOp",EDGE,"E5.1.19.0")]});var subQ5=makeQuery(id+"F0.imprint","INTERSECT",VERTEX,{"derivedFrom":[subQ0,sQuery(id+"F0.wireOp",EDGE,"E6.1.20.0")]});var subQ6=makeQuery(id+"F0.imprint","INTERSECT",VERTEX,{"derivedFrom":[subQ0,sQuery(id+"F0.wireOp",EDGE,"E6.1.21.0")]});var subQ7=makeQuery(id+"F0.imprint","INTERSECT",VERTEX,{"derivedFrom":[subQ0,sQuery(id+"F0.wireOp",EDGE,"E6.1.22.0")]});Q0=makeQuery(id+"F2.opExtrude","CAP_EDGE",EDGE,{"disambiguationData":[OSD([subQ0]),TDD([makeQuery(id+"F0.imprint","IMPRINT",EDGE,{"disambiguationData":[TD([[subQ1,1.0]])],"derivedFrom":subQ0}),makeQuery(id+"F0.imprint","IMPRINT",EDGE,{"disambiguationData":[TD([[subQ1,-1.0]])],"derivedFrom":subQ0}),makeQuery(id+"F0.imprint","IMPRINT",EDGE,{"disambiguationData":[TD([[subQ2,-1.0]])],"derivedFrom":subQ0}),makeQuery(id+"F0.imprint","IMPRINT",EDGE,{"disambiguationData":[TD([[subQ3,-1.0]])],"derivedFrom":subQ0}),makeQuery(id+"F0.imprint","IMPRINT",EDGE,{"disambiguationData":[TD([[subQ4,-1.0]])],"derivedFrom":subQ0}),makeQuery(id+"F0.imprint","IMPRINT",EDGE,{"disambiguationData":[TD([[subQ5,-1.0]])],"derivedFrom":subQ0}),makeQuery(id+"F0.imprint","IMPRINT",EDGE,{"disambiguationData":[TD([[subQ6,-1.0]])],"derivedFrom":subQ0}),makeQuery(id+"F0.imprint","IMPRINT",EDGE,{"disambiguationData":[TD([[subQ7,-1.0]])],"derivedFrom":subQ0})])],"isStart":false});}
            var Q1;
            {var subQ0=sQuery(id+"F0.wireOp",EDGE,"E2.0");var subQ1=makeQuery(id+"F0.imprint","INTERSECT",VERTEX,{"derivedFrom":[subQ0,sQuery(id+"F0.wireOp",EDGE,"E7.1.25.0")]});var subQ2=makeQuery(id+"F0.imprint","INTERSECT",VERTEX,{"derivedFrom":[subQ0,sQuery(id+"F0.wireOp",EDGE,"E8.1.26.0")]});var subQ3=makeQuery(id+"F0.imprint","INTERSECT",VERTEX,{"derivedFrom":[subQ0,sQuery(id+"F0.wireOp",EDGE,"E8.1.27.0")]});var subQ4=makeQuery(id+"F0.imprint","INTERSECT",VERTEX,{"derivedFrom":[subQ0,sQuery(id+"F0.wireOp",EDGE,"E8.1.28.0")]});var subQ5=makeQuery(id+"F0.imprint","INTERSECT",VERTEX,{"derivedFrom":[subQ0,sQuery(id+"F0.wireOp",EDGE,"E8.1.29.0")]});var subQ6=makeQuery(id+"F0.imprint","INTERSECT",VERTEX,{"derivedFrom":[subQ0,sQuery(id+"F0.wireOp",EDGE,"E9.1.30.0")]});var subQ7=makeQuery(id+"F0.imprint","INTERSECT",VERTEX,{"derivedFrom":[subQ0,sQuery(id+"F0.wireOp",EDGE,"E9.1.31.0")]});Q1=makeQuery(id+"F2.opExtrude","CAP_EDGE",EDGE,{"disambiguationData":[OSD([subQ0]),TDD([makeQuery(id+"F0.imprint","IMPRINT",EDGE,{"disambiguationData":[TD([[subQ1,1.0]])],"derivedFrom":subQ0}),makeQuery(id+"F0.imprint","IMPRINT",EDGE,{"disambiguationData":[TD([[subQ1,-1.0]])],"derivedFrom":subQ0}),makeQuery(id+"F0.imprint","IMPRINT",EDGE,{"disambiguationData":[TD([[subQ2,-1.0]])],"derivedFrom":subQ0}),makeQuery(id+"F0.imprint","IMPRINT",EDGE,{"disambiguationData":[TD([[subQ3,-1.0]])],"derivedFrom":subQ0}),makeQuery(id+"F0.imprint","IMPRINT",EDGE,{"disambiguationData":[TD([[subQ4,-1.0]])],"derivedFrom":subQ0}),makeQuery(id+"F0.imprint","IMPRINT",EDGE,{"disambiguationData":[TD([[subQ5,-1.0]])],"derivedFrom":subQ0}),makeQuery(id+"F0.imprint","IMPRINT",EDGE,{"disambiguationData":[TD([[subQ6,-1.0]])],"derivedFrom":subQ0}),makeQuery(id+"F0.imprint","IMPRINT",EDGE,{"disambiguationData":[TD([[subQ7,-1.0]])],"derivedFrom":subQ0})])],"isStart":false});}
            var Q2;
            {var subQ0=sQuery(id+"F0.wireOp",EDGE,"E2.0");var subQ1=makeQuery(id+"F0.imprint","INTERSECT",VERTEX,{"derivedFrom":[subQ0,sQuery(id+"F0.wireOp",EDGE,"E10.1.35.0")]});var subQ2=makeQuery(id+"F0.imprint","INTERSECT",VERTEX,{"derivedFrom":[subQ0,sQuery(id+"F0.wireOp",EDGE,"E9.1.34.0")]});var subQ3=makeQuery(id+"F0.imprint","INTERSECT",VERTEX,{"derivedFrom":[subQ0,sQuery(id+"F0.wireOp",EDGE,"E10.1.36.0")]});var subQ4=makeQuery(id+"F0.imprint","INTERSECT",VERTEX,{"derivedFrom":[subQ0,sQuery(id+"F0.wireOp",EDGE,"E10.1.37.0")]});var subQ5=makeQuery(id+"F0.imprint","INTERSECT",VERTEX,{"derivedFrom":[subQ0,sQuery(id+"F0.wireOp",EDGE,"E10.1.38.0")]});var subQ6=makeQuery(id+"F0.imprint","INTERSECT",VERTEX,{"derivedFrom":[subQ0,sQuery(id+"F0.wireOp",EDGE,"E10.1.39.0")]});var subQ7=makeQuery(id+"F0.imprint","INTERSECT",VERTEX,{"derivedFrom":[subQ0,sQuery(id+"F0.wireOp",EDGE,"E14.1.40.0")]});Q2=makeQuery(id+"F2.opExtrude","CAP_EDGE",EDGE,{"disambiguationData":[OSD([subQ0]),TDD([makeQuery(id+"F0.imprint","IMPRINT",EDGE,{"disambiguationData":[TD([[subQ2,-1.0]])],"derivedFrom":subQ0}),makeQuery(id+"F0.imprint","IMPRINT",EDGE,{"disambiguationData":[TD([[subQ1,-1.0]])],"derivedFrom":subQ0}),makeQuery(id+"F0.imprint","IMPRINT",EDGE,{"disambiguationData":[TD([[subQ3,-1.0]])],"derivedFrom":subQ0}),makeQuery(id+"F0.imprint","IMPRINT",EDGE,{"disambiguationData":[TD([[subQ4,-1.0]])],"derivedFrom":subQ0}),makeQuery(id+"F0.imprint","IMPRINT",EDGE,{"disambiguationData":[TD([[subQ5,-1.0]])],"derivedFrom":subQ0}),makeQuery(id+"F0.imprint","IMPRINT",EDGE,{"disambiguationData":[TD([[subQ6,-1.0]])],"derivedFrom":subQ0}),makeQuery(id+"F0.imprint","IMPRINT",EDGE,{"disambiguationData":[TD([[subQ7,-1.0]])],"derivedFrom":subQ0}),makeQuery(id+"F0.imprint","IMPRINT",EDGE,{"disambiguationData":[TD([[subQ2,1.0]])],"derivedFrom":subQ0})])],"isStart":false});}
            var Q3;
            {var subQ0=sQuery(id+"F0.wireOp",EDGE,"E2.0");var subQ1=makeQuery(id+"F0.imprint","INTERSECT",VERTEX,{"derivedFrom":[subQ0,sQuery(id+"F0.wireOp",EDGE,"E14.1.43.0")]});var subQ3=makeQuery(id+"F0.imprint","INTERSECT",VERTEX,{"derivedFrom":[subQ0,sQuery(id+"F0.wireOp",EDGE,"E3")]});var subQ4=makeQuery(id+"F0.imprint","INTERSECT",VERTEX,{"derivedFrom":[subQ0,sQuery(id+"F0.wireOp",EDGE,"E4.1.0")]});var subQ5=makeQuery(id+"F0.imprint","INTERSECT",VERTEX,{"derivedFrom":[subQ0,sQuery(id+"F0.wireOp",EDGE,"E4.2.0")]});var subQ6=makeQuery(id+"F0.imprint","INTERSECT",VERTEX,{"derivedFrom":[subQ0,sQuery(id+"F0.wireOp",EDGE,"E4.3.0")]});var subQ7=makeQuery(id+"F0.imprint","INTERSECT",VERTEX,{"derivedFrom":[subQ0,sQuery(id+"F0.wireOp",EDGE,"E4.4.0")]});Q3=makeQuery(id+"F2.opExtrude","CAP_EDGE",EDGE,{"disambiguationData":[OSD([subQ0]),TDD([makeQuery(id+"F0.imprint","IMPRINT",EDGE,{"disambiguationData":[TD([[subQ1,1.0]])],"derivedFrom":subQ0}),makeQuery(id+"F0.imprint","IMPRINT",EDGE,{"disambiguationData":[TD([[subQ1,-1.0]])],"derivedFrom":subQ0}),makeQuery(id+"F0.imprint","IMPRINT",EDGE,{"disambiguationData":[TD([[subQ3,1.0]])],"derivedFrom":subQ0}),makeQuery(id+"F0.imprint","IMPRINT",EDGE,{"disambiguationData":[TD([[subQ3,-1.0]])],"derivedFrom":subQ0}),makeQuery(id+"F0.imprint","IMPRINT",EDGE,{"disambiguationData":[TD([[subQ4,-1.0]])],"derivedFrom":subQ0}),makeQuery(id+"F0.imprint","IMPRINT",EDGE,{"disambiguationData":[TD([[subQ5,-1.0]])],"derivedFrom":subQ0}),makeQuery(id+"F0.imprint","IMPRINT",EDGE,{"disambiguationData":[TD([[subQ6,-1.0]])],"derivedFrom":subQ0}),makeQuery(id+"F0.imprint","IMPRINT",EDGE,{"disambiguationData":[TD([[subQ7,-1.0]])],"derivedFrom":subQ0})])],"isStart":false});}
            var Q4;
            {var subQ0=sQuery(id+"F0.wireOp",EDGE,"E2.0");var subQ1=makeQuery(id+"F0.imprint","INTERSECT",VERTEX,{"derivedFrom":[subQ0,sQuery(id+"F0.wireOp",EDGE,"E4.7.0")]});var subQ2=makeQuery(id+"F0.imprint","INTERSECT",VERTEX,{"derivedFrom":[subQ0,sQuery(id+"F0.wireOp",EDGE,"E4.8.0")]});var subQ3=makeQuery(id+"F0.imprint","INTERSECT",VERTEX,{"derivedFrom":[subQ0,sQuery(id+"F0.wireOp",EDGE,"E4.9.0")]});var subQ4=makeQuery(id+"F0.imprint","INTERSECT",VERTEX,{"derivedFrom":[subQ0,sQuery(id+"F0.wireOp",EDGE,"E5.1.10.0")]});var subQ5=makeQuery(id+"F0.imprint","INTERSECT",VERTEX,{"derivedFrom":[subQ0,sQuery(id+"F0.wireOp",EDGE,"E5.1.11.0")]});var subQ6=makeQuery(id+"F0.imprint","INTERSECT",VERTEX,{"derivedFrom":[subQ0,sQuery(id+"F0.wireOp",EDGE,"E5.1.12.0")]});var subQ7=makeQuery(id+"F0.imprint","INTERSECT",VERTEX,{"derivedFrom":[subQ0,sQuery(id+"F0.wireOp",EDGE,"E5.1.13.0")]});Q4=makeQuery(id+"F2.opExtrude","CAP_EDGE",EDGE,{"disambiguationData":[OSD([subQ0]),TDD([makeQuery(id+"F0.imprint","IMPRINT",EDGE,{"disambiguationData":[TD([[subQ1,1.0]])],"derivedFrom":subQ0}),makeQuery(id+"F0.imprint","IMPRINT",EDGE,{"disambiguationData":[TD([[subQ1,-1.0]])],"derivedFrom":subQ0}),makeQuery(id+"F0.imprint","IMPRINT",EDGE,{"disambiguationData":[TD([[subQ2,-1.0]])],"derivedFrom":subQ0}),makeQuery(id+"F0.imprint","IMPRINT",EDGE,{"disambiguationData":[TD([[subQ3,-1.0]])],"derivedFrom":subQ0}),makeQuery(id+"F0.imprint","IMPRINT",EDGE,{"disambiguationData":[TD([[subQ4,-1.0]])],"derivedFrom":subQ0}),makeQuery(id+"F0.imprint","IMPRINT",EDGE,{"disambiguationData":[TD([[subQ5,-1.0]])],"derivedFrom":subQ0}),makeQuery(id+"F0.imprint","IMPRINT",EDGE,{"disambiguationData":[TD([[subQ6,-1.0]])],"derivedFrom":subQ0}),makeQuery(id+"F0.imprint","IMPRINT",EDGE,{"disambiguationData":[TD([[subQ7,-1.0]])],"derivedFrom":subQ0})])],"isStart":false});}
            chamfer(context, id + "F5", {"entities" : qUnion([Q0, Q1, Q2, Q3, Q4]), "width" : 1 * mm});
        }
        {
            var Q0;
            {var subQ0=sQuery(id+"F0.wireOp",EDGE,"E0");var subQ1=makeQuery(id+"F0.imprint","INTERSECT",VERTEX,{"derivedFrom":[subQ0,sQuery(id+"F0.wireOp",EDGE,"E3")]});var subQ2=makeQuery(id+"F0.imprint","INTERSECT",VERTEX,{"derivedFrom":[subQ0,sQuery(id+"F0.wireOp",EDGE,"E4.1.0")]});Q0=makeQuery(id+"F3.boolean.opBoolean","COPY",EDGE,{"derivedFrom":makeQuery(id+"F3.opExtrude","CAP_EDGE",EDGE,{"disambiguationData":[OSD([subQ0]),TDD([makeQuery(id+"F0.imprint","IMPRINT",EDGE,{"disambiguationData":[TD([[makeQuery(id+"F0.imprint","INTERSECT",VERTEX,{"derivedFrom":[subQ0,sQuery(id+"F0.wireOp",EDGE,"E14.1.44.0")]}),-1.0]])],"derivedFrom":subQ0}),makeQuery(id+"F0.imprint","IMPRINT",EDGE,{"disambiguationData":[TD([[subQ1,-1.0]])],"derivedFrom":subQ0}),makeQuery(id+"F0.imprint","IMPRINT",EDGE,{"disambiguationData":[TD([[subQ2,-1.0]])],"derivedFrom":subQ0})])],"isStart":false})});}
            var Q1;
            {var subQ0=sQuery(id+"F0.wireOp",EDGE,"E0");var subQ1=makeQuery(id+"F0.imprint","INTERSECT",VERTEX,{"derivedFrom":[subQ0,sQuery(id+"F0.wireOp",EDGE,"E10.1.36.0")]});var subQ2=makeQuery(id+"F0.imprint","INTERSECT",VERTEX,{"derivedFrom":[subQ0,sQuery(id+"F0.wireOp",EDGE,"E10.1.37.0")]});Q1=makeQuery(id+"F3.boolean.opBoolean","COPY",EDGE,{"derivedFrom":makeQuery(id+"F3.opExtrude","CAP_EDGE",EDGE,{"disambiguationData":[OSD([subQ0]),TDD([makeQuery(id+"F0.imprint","IMPRINT",EDGE,{"disambiguationData":[TD([[makeQuery(id+"F0.imprint","INTERSECT",VERTEX,{"derivedFrom":[subQ0,sQuery(id+"F0.wireOp",EDGE,"E10.1.35.0")]}),-1.0]])],"derivedFrom":subQ0}),makeQuery(id+"F0.imprint","IMPRINT",EDGE,{"disambiguationData":[TD([[subQ1,-1.0]])],"derivedFrom":subQ0}),makeQuery(id+"F0.imprint","IMPRINT",EDGE,{"disambiguationData":[TD([[subQ2,-1.0]])],"derivedFrom":subQ0})])],"isStart":false})});}
            var Q2;
            {var subQ0=sQuery(id+"F0.wireOp",EDGE,"E0");var subQ1=makeQuery(id+"F0.imprint","INTERSECT",VERTEX,{"derivedFrom":[subQ0,sQuery(id+"F0.wireOp",EDGE,"E8.1.27.0")]});var subQ2=makeQuery(id+"F0.imprint","INTERSECT",VERTEX,{"derivedFrom":[subQ0,sQuery(id+"F0.wireOp",EDGE,"E8.1.28.0")]});Q2=makeQuery(id+"F3.boolean.opBoolean","COPY",EDGE,{"derivedFrom":makeQuery(id+"F3.opExtrude","CAP_EDGE",EDGE,{"disambiguationData":[OSD([subQ0]),TDD([makeQuery(id+"F0.imprint","IMPRINT",EDGE,{"disambiguationData":[TD([[makeQuery(id+"F0.imprint","INTERSECT",VERTEX,{"derivedFrom":[subQ0,sQuery(id+"F0.wireOp",EDGE,"E8.1.26.0")]}),-1.0]])],"derivedFrom":subQ0}),makeQuery(id+"F0.imprint","IMPRINT",EDGE,{"disambiguationData":[TD([[subQ1,-1.0]])],"derivedFrom":subQ0}),makeQuery(id+"F0.imprint","IMPRINT",EDGE,{"disambiguationData":[TD([[subQ2,-1.0]])],"derivedFrom":subQ0})])],"isStart":false})});}
            var Q3;
            {var subQ0=sQuery(id+"F0.wireOp",EDGE,"E0");var subQ1=makeQuery(id+"F0.imprint","INTERSECT",VERTEX,{"derivedFrom":[subQ0,sQuery(id+"F0.wireOp",EDGE,"E5.1.18.0")]});var subQ2=makeQuery(id+"F0.imprint","INTERSECT",VERTEX,{"derivedFrom":[subQ0,sQuery(id+"F0.wireOp",EDGE,"E5.1.19.0")]});Q3=makeQuery(id+"F3.boolean.opBoolean","COPY",EDGE,{"derivedFrom":makeQuery(id+"F3.opExtrude","CAP_EDGE",EDGE,{"disambiguationData":[OSD([subQ0]),TDD([makeQuery(id+"F0.imprint","IMPRINT",EDGE,{"disambiguationData":[TD([[makeQuery(id+"F0.imprint","INTERSECT",VERTEX,{"derivedFrom":[subQ0,sQuery(id+"F0.wireOp",EDGE,"E5.1.17.0")]}),-1.0]])],"derivedFrom":subQ0}),makeQuery(id+"F0.imprint","IMPRINT",EDGE,{"disambiguationData":[TD([[subQ1,-1.0]])],"derivedFrom":subQ0}),makeQuery(id+"F0.imprint","IMPRINT",EDGE,{"disambiguationData":[TD([[subQ2,-1.0]])],"derivedFrom":subQ0})])],"isStart":false})});}
            var Q4;
            {var subQ0=sQuery(id+"F0.wireOp",EDGE,"E0");var subQ1=makeQuery(id+"F0.imprint","INTERSECT",VERTEX,{"derivedFrom":[subQ0,sQuery(id+"F0.wireOp",EDGE,"E4.9.0")]});var subQ2=makeQuery(id+"F0.imprint","INTERSECT",VERTEX,{"derivedFrom":[subQ0,sQuery(id+"F0.wireOp",EDGE,"E5.1.10.0")]});Q4=makeQuery(id+"F3.boolean.opBoolean","COPY",EDGE,{"derivedFrom":makeQuery(id+"F3.opExtrude","CAP_EDGE",EDGE,{"disambiguationData":[OSD([subQ0]),TDD([makeQuery(id+"F0.imprint","IMPRINT",EDGE,{"disambiguationData":[TD([[makeQuery(id+"F0.imprint","INTERSECT",VERTEX,{"derivedFrom":[subQ0,sQuery(id+"F0.wireOp",EDGE,"E4.8.0")]}),-1.0]])],"derivedFrom":subQ0}),makeQuery(id+"F0.imprint","IMPRINT",EDGE,{"disambiguationData":[TD([[subQ1,-1.0]])],"derivedFrom":subQ0}),makeQuery(id+"F0.imprint","IMPRINT",EDGE,{"disambiguationData":[TD([[subQ2,-1.0]])],"derivedFrom":subQ0})])],"isStart":false})});}
            chamfer(context, id + "F6", {"entities" : qUnion([Q0, Q1, Q2, Q3, Q4]), "chamferType" : ChamferType.OFFSET_ANGLE, "width" : 3 * mm, "oppositeDirection" : false, "angle" : 32 * degree, "tangentPropagation" : true});
        }
    });
